# Revit family: Lighting_Floor-Mounted_Zero_Silo_Floor
name_source: partatom
category: Lighting Fixtures
units: mm (PartAtom-declared; Revit-internal decimal feet)

## family parameters
Always vertical = Yes
Cut with Voids When Loaded = No
Light Source = Yes
OmniClass Number = 23.80.70.00
OmniClass Title = Lighting
Part Type = Normal
Room Calculation Point = No
Round Connector Dimension = Use Diameter
Shared = No
Work Plane-Based = No

## types (7) — shared parameters
AssetType = Movable
BIMObjectName = Lighting_Floor-Mounted_Zero_Silo_Floor
Brand = Zero
Brand url = http://www.zero.se
Category = Floor
Collection = Silo
Color Filter = 16777215
Design country = Sweden
Designer = Note Design Studio
Dimming Lamp Color Temperature Shift = <None>
DurationUnit = Year
Edition number = 1
Features = Connection: 2,5 m cable and plug with switch on the cable.
Finish = Painted aluminum and steel
HasProtectiveEarth = No
IP_Code = IP20
IfcExportAs = IfcLightFixtureType
IfcExportType = NOTDEFINED
LightFixtureMountingType = Surface
LightFixturePlacingType = Floor
LightFixtureSecondaryMaterial = Stainless Steel, Polished
Manufacturer = Zero
Manufacturer country = Sweden
Manufacturer name = ZERO
ManufacturerName = Zero
ManufacturerURL = https://www.zerolighting.com
Material = Aluminium and steel
Material main = Aluminium
Material secondary = Steel
NBSDescription = General purpose luminaires
NBSReference = 90-60-45/405
Name = Zero_Silo_Floor
Nominal height = 1340 mm  [stored 4.39633 ft]
Nominal width = 250 mm  [stored 0.82021 ft]
NominalCurrent = 0 A
NominalDiameter = 250 mm  [stored 0.82021 ft]
NominalFrequencyRange = 50 Hz
NominalLength = 250 mm  [stored 0.82021 ft]
NominalRadius = 125 mm  [stored 0.410105 ft]
NominalVoltage = 230 V
NominalVoltageCalc = 0 V
NumberOfPoles = 1
PhaseAngle = 0.00°
Photometric Web File = Silo8205-LED_IES.IES
Product Guid = 518e2963-2a1a-4f5f-b5f5-f2a1cb1a37ce
Product SKU = Silo_floor_fixture
Product family = Silo
Product group = Floor fixture
Revision = 5
Shape = Sculptured
Size = 250x250x1340 mm
Tilt Angle = 90.00°
TotalWattage = 50 W
URL = https://www.zerolighting.com
Uniclass2 = Pr_70_70_48_32
Uniclass2015Description = Free standing luminaires
Uniclass2015Reference = Pr_70_70_48_32
UsageCurrent = 0 A
Version = 3
VersionDate = 31/08/2023
WarrantyDurationUnit = Year
Weight Net (Kg) = 3.5
zero-valued in all types: Default Elevation, DefaultElevation, ElectricalDeviceNominalPower, MaintenanceFactor, NumberOfSources

## per-type parameters (varying)
| type | ArticleNumber | Color | LightFixtureMainMaterial | ModelNumber |
| Silo Floor Max 50W/E27 White | 8208-1-01 | White | White RAL 9010 | 8208-1-01 |
| Silo Floor Max 50W/E27 Black | 8208-1-06 | Black | Black RAL 9005 | 8208-1-06 |
| Silo Floor Max 50W/E27 Grey | 8208-1-11 | Grey | Grey RAL 7030 | 8208-1-11 |
| Silo Floor Max 50W/E27 Green | 8208-1-12 | Green | Green RAL 6021 | 8208-1-12 |
| Silo Floor Max 50W/E27 Yellow | 8208-1-14 | Yellow | Yellow RAL 1018 | 8208-1-14 |
| Silo Floor Max 50W/E27 Apricot | 8208-1-17 | Apricot | Apricot RAL 3012 | 8208-1-17 |
| Silo Floor Max 50W/E27 Ivory | 8208-1-46 | Ivory | Ivory RAL 1015 | 8208-1-46 |

note: column(s) folded — value = type name in every type: Model

note: [stored X ft] marks values corroborated as IEEE doubles in the binary element streams (Revit-internal decimal feet)

## geometry (parser evidence)
native form markers: Sweep x6
no freeform markers — native parametric forms only
